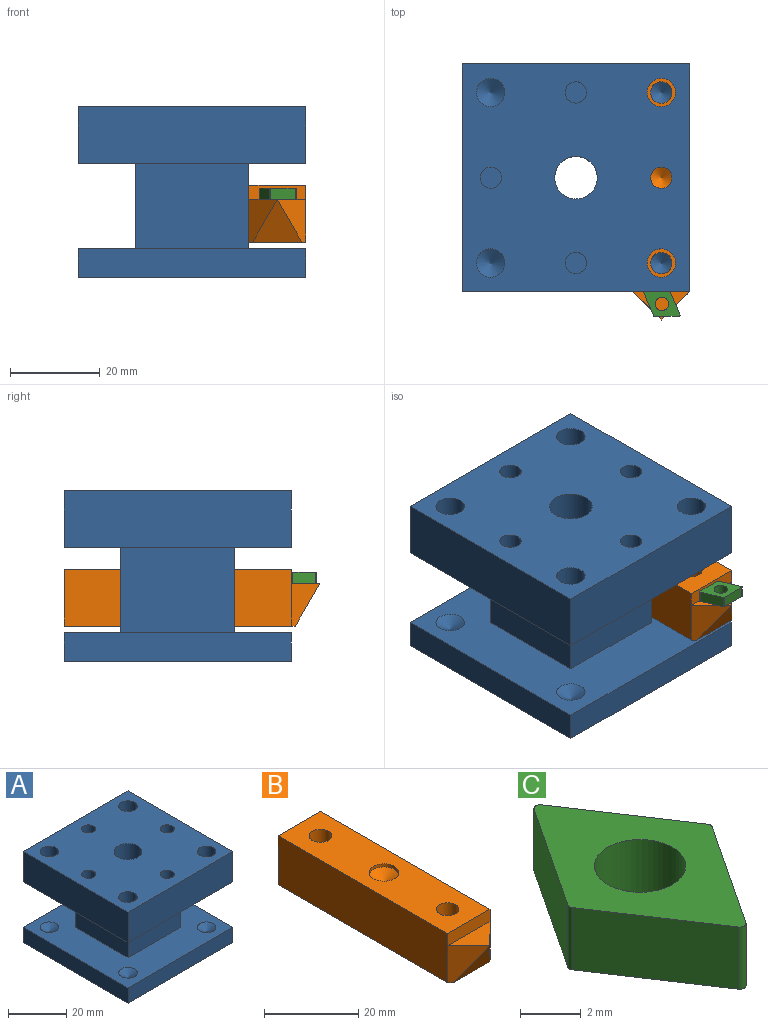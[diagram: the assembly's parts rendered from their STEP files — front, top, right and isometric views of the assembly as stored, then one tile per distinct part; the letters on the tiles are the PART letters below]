
ASSEMBLY  parts=3 mates=2
PART A: 29 faces, bbox 50.8x50.8x38.1 mm
  f0: plane 25.4x19.05mm, normal (0,1,0), area 483.9mm2, adj f1,f3,f8,f14
  f1: plane 25.4x19.05mm, normal (-1,0,0), area 483.9mm2, adj f0,f2,f8,f14
  f2: plane 25.4x19.05mm, normal (0,-1,0), area 483.9mm2, adj f1,f3,f8,f14
  f3: plane 25.4x19.05mm, normal (1,0,0), area 483.9mm2, adj f0,f2,f8,f14
  f4: plane 50.8x6.35mm, normal (-1,0,0), area 322.6mm2, adj f5,f7,f8,f9
  f5: plane 50.8x6.35mm, normal (0,-1,0), area 322.6mm2, adj f4,f6,f8,f9
  f6: plane 50.8x6.35mm, normal (1,0,0), area 322.6mm2, adj f5,f7,f8,f9
  f7: plane 50.8x6.35mm, normal (0,1,0), area 322.6mm2, adj f4,f6,f8,f9
  f8: plane 50.8x50.8mm, normal (0,0,1), area 1808.8mm2, adj f0,f1,f2,f3,f4,f5,f6,f7
  f9: plane 50.8x50.8mm, normal (0,0,-1), area 2509.4mm2, adj f4,f5,f6,f7,f16
  f10: plane 50.8x12.7mm, normal (-1,0,0), area 645.2mm2, adj f11,f13,f14,f15
  f11: plane 50.8x12.7mm, normal (0,-1,0), area 645.2mm2, adj f10,f12,f14,f15
  f12: plane 50.8x12.7mm, normal (1,0,0), area 645.2mm2, adj f11,f13,f14,f15
  f13: plane 50.8x12.7mm, normal (0,1,0), area 645.2mm2, adj f10,f12,f14,f15
  f14: plane 50.8x50.8mm, normal (0,0,-1), area 1737.2mm2, adj f0,f1,f2,f3,f10,f11,f12,f13
  f15: plane 50.8x50.8mm, normal (0,0,1), area 2311.1mm2, adj f10,f11,f12,f13,f16,f17,f18,f19
  f16: cylinder r=4.76mm len=38.1mm, axis (0,0,1), area 1140.1mm2, adj f9,f15
  f17: cylinder r=2.39mm len=12.7mm, axis (0,0,1), area 190.5mm2, adj f14,f15
  f18: cylinder r=2.39mm len=12.7mm, axis (0,0,1), area 190.5mm2, adj f14,f15
  f19: cylinder r=2.39mm len=12.7mm, axis (0,0,1), area 190.5mm2, adj f14,f15
  f20: cylinder r=2.39mm len=12.7mm, axis (0,0,1), area 190.5mm2, adj f14,f15
  f21: cylinder r=3.17mm len=12.7mm, axis (0,0,1), area 253.4mm2, adj f14,f15
  f22: cylinder r=3.17mm len=12.7mm, axis (0,0,1), area 253.4mm2, adj f14,f15
  f23: cylinder r=3.17mm len=12.7mm, axis (0,0,1), area 253.4mm2, adj f14,f15
  f24: cylinder r=3.17mm len=12.7mm, axis (0,0,1), area 253.4mm2, adj f14,f15
  f25: cone r=0mm half-angle=59deg, axis (0,0,1), area 36.9mm2, adj f8
  f26: cone r=0mm half-angle=59deg, axis (0,0,1), area 36.9mm2, adj f8
  f27: cone r=0mm half-angle=59deg, axis (0,0,1), area 36.9mm2, adj f8
  f28: cone r=0mm half-angle=59deg, axis (0,0,1), area 36.9mm2, adj f8
PART B: 14 faces, bbox 12.7x57.2x12.7 mm
  f0: plane 12.7x6.35mm, normal (0,0,1), area 40.3mm2, adj f5,f8,f9
  f1: plane 11x9.53mm, normal (0,-0.87,-0.5), area 60.5mm2, adj f2,f8,f9
  f2: plane 51.65x12.7mm, normal (0,0,-1), area 619.4mm2, adj f1,f3,f6,f7,f8,f9,f12,f13
  f3: plane 12.7x12.7mm, normal (0,1,0), area 161.3mm2, adj f2,f4,f6,f7
  f4: plane 50.8x12.7mm, normal (0,0,1), area 577.7mm2, adj f3,f5,f6,f7,f11,f12,f13
  f5: plane 12.7x3.18mm, normal (0,-1,0), area 40.3mm2, adj f0,f4,f6,f7
  f6: plane 50.8x12.7mm, normal (1,0,0), area 645.2mm2, adj f2,f3,f4,f5,f9
  f7: plane 50.8x12.7mm, normal (-1,0,0), area 645.2mm2, adj f2,f3,f4,f5,f8
  f8: plane 9.53x6.35mm, normal (-0.71,-0.71,0), area 48.5mm2, adj f0,f1,f2,f7
  f9: plane 9.53x6.35mm, normal (0.71,-0.71,0), area 48.5mm2, adj f0,f1,f2,f6
  f10: cone r=0mm half-angle=59deg, axis (0,0,1), area 36.9mm2, adj f11
  f11: cylinder r=3.17mm len=6.35mm, axis (0,0,1), area 15.7mm2, adj f4,f10
  f12: cylinder r=2.39mm len=12.7mm, axis (0,0,1), area 190.5mm2, adj f2,f4
  f13: cylinder r=2.39mm len=12.7mm, axis (0,0,1), area 190.5mm2, adj f2,f4
PART C: 11 faces, bbox 6.6x9.7x2.5 mm
  f0: plane 4.63x3.07mm, normal (-0.83,0.55,0), area 13.9mm2, adj f5,f6,f7,f10
  f1: plane 4.63x3.07mm, normal (-0.83,-0.55,0), area 13.9mm2, adj f5,f6,f7,f8
  f2: plane 4.63x3.07mm, normal (0.83,-0.55,0), area 13.9mm2, adj f5,f6,f8,f9
  f3: plane 4.63x3.07mm, normal (0.83,0.55,0), area 13.9mm2, adj f5,f6,f9,f10
  f4: cylinder r=1.5mm len=3mm, axis (0,0,-1), area 23.6mm2, adj f5,f6
  f5: plane 9.67x6.55mm, normal (0,0,1), area 26mm2, adj f0,f1,f2,f3,f4,f7,f8,f9
  f6: plane 9.67x6.55mm, normal (0,0,-1), area 26mm2, adj f0,f1,f2,f3,f4,f7,f8,f9
  f7: cylinder r=0.2mm len=2.5mm, axis (0,0,-1), area 0.6mm2, adj f0,f1,f5,f6
  f8: cylinder r=0.2mm len=2.5mm, axis (0,0,-1), area 1mm2, adj f1,f2,f5,f6
  f9: cylinder r=0.2mm len=2.5mm, axis (0,0,-1), area 0.6mm2, adj f2,f3,f5,f6
  f10: cylinder r=0.2mm len=2.5mm, axis (0,0,-1), area 1mm2, adj f0,f3,f5,f6
PLACE A at identity
PLACE B t=(38.1,-6.35,17.38)mm
PLACE C rot(axis=(0,0,1),56.4deg) t=(42.77,-5.53,17.38)mm
MATE slider A.f22 <-> B.f13  axis (0,0,1) through (44.45,6.35,38.1)mm
MATE planar B.f0 <-> C.f4  axis (0,0,1) through (44.45,-2.12,17.38)mm
